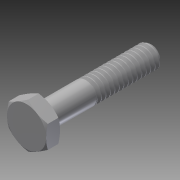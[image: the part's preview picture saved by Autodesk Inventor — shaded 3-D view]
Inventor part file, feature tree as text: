
AUTODESK INVENTOR PART (.ipt)
format: ipt  version: 2014 SP1 (Build 180222100, 222)  size: 474,112 bytes
history: native  units: in
note: dims shown in document units (in); Inventor stores cm internally (conversion verified against a paired STEP export)
features: extrude x1, other x1, imported_body x1
ambient origin geometry x8: Origin, YZ Plane, XZ Plane, XY Plane, X Axis, Y Axis, Z Axis, Center Point
bodies: Body1 (feature_tree)
feature tree (3):
  extrude  "Extrude14"  [1 undecoded]
  other  "91257A5441"
  imported_body  "Base1"
note: 1 required parameter value undecoded (feature->parameter linkage not recoverable at this tier; creation-order binding heuristic only, values carry confidence <= 0.55)
